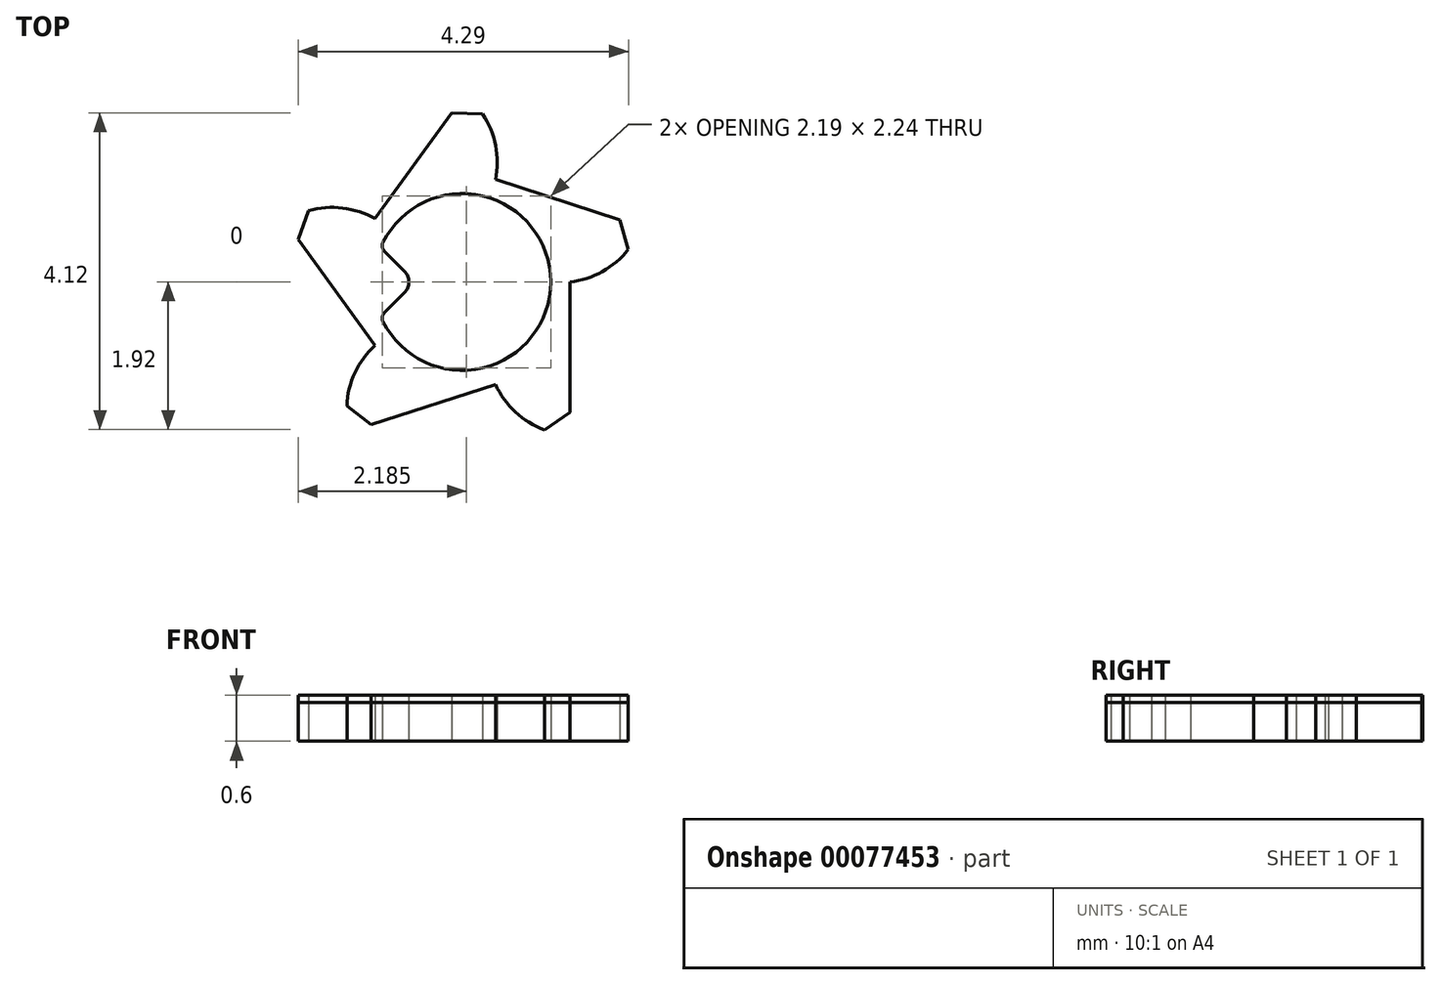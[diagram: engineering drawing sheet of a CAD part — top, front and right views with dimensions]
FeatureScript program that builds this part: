
annotation { "Feature Type Name" : "Feature", "Feature Type Description" : "" }
export const myFeature = defineFeature(function(context is Context, id is Id, definition is map)
    precondition{}
    {
        {
            var Q0;
            Q0=qCreatedBy(makeId("Top.planeOp"),FACE);
            var sketch = newSketch(context, id + "F0", { "sketchPlane" : qUnion([Q0])});
            skCircle(sketch, "E0", {"center": v(0, 0) * mm, "radius": 1.4 * mm, "construction": true});
            skCircle(sketch, "E1", {"center": v(0, 0) * mm, "radius": 1.65 * mm, "construction": true});
            skCircle(sketch, "E2", {"center": v(0, 0) * mm, "radius": 2.2 * mm, "construction": true});
            skArc(sketch, "E3", {"start": v(-1.03, -0.51) * mm, "mid": v(1.15, 0) * mm, "end": v(-1.03, 0.51) * mm});
            skLineSegment(sketch, "E4", {"start": v(0, 0) * mm, "end": v(1.4, 0) * mm, "construction": true});
            skLineSegment(sketch, "E5", {"start": v(0, 0) * mm, "end": v(0.43, -1.33) * mm, "construction": true});
            skLineSegment(sketch, "E6", {"start": v(0, 0) * mm, "end": v(-1.13, -0.82) * mm, "construction": true});
            skLineSegment(sketch, "E7", {"start": v(0, 0) * mm, "end": v(-1.13, 0.82) * mm, "construction": true});
            skLineSegment(sketch, "E8", {"start": v(0, 0) * mm, "end": v(0.43, 1.33) * mm, "construction": true});
            skLineSegment(sketch, "E9", {"start": v(1.4, 0) * mm, "end": v(1.4, -1.7) * mm});
            skLineSegment(sketch, "E10", {"start": v(1.4, -1.7) * mm, "end": v(1.07, -1.92) * mm});
            skLineSegment(sketch, "E11", {"start": v(0.43, -1.33) * mm, "end": v(-1.18, -1.86) * mm});
            skLineSegment(sketch, "E12", {"start": v(-1.18, -1.86) * mm, "end": v(-1.5, -1.61) * mm});
            skLineSegment(sketch, "E13", {"start": v(-1.13, -0.82) * mm, "end": v(-2.13, 0.55) * mm});
            skLineSegment(sketch, "E14", {"start": v(-2.13, 0.55) * mm, "end": v(-2, 0.93) * mm});
            skLineSegment(sketch, "E15", {"start": v(-1.13, 0.82) * mm, "end": v(-0.14, 2.2) * mm});
            skLineSegment(sketch, "E16", {"start": v(-0.14, 2.2) * mm, "end": v(0.26, 2.18) * mm});
            skLineSegment(sketch, "E17", {"start": v(0.43, 1.33) * mm, "end": v(2.05, 0.8) * mm});
            skLineSegment(sketch, "E18", {"start": v(2.05, 0.8) * mm, "end": v(2.16, 0.42) * mm});
            skArc(sketch, "E19", {"start": v(0.43, -1.33) * mm, "mid": v(0.7, -1.7) * mm, "end": v(1.07, -1.92) * mm});
            skPoint(sketch, "E19.third.point", {"position": v(0.36, -1.1) * mm});
            skArc(sketch, "E20", {"start": v(-1.13, -0.82) * mm, "mid": v(-1.4, -1.18) * mm, "end": v(-1.5, -1.61) * mm});
            skPoint(sketch, "E20.third.point", {"position": v(-0.93, -0.68) * mm});
            skPoint(sketch, "E21.third.point", {"position": v(-0.93, 0.68) * mm});
            skPoint(sketch, "E22.third.point", {"position": v(0.36, 1.1) * mm});
            skArc(sketch, "E23", {"start": v(1.4, 0) * mm, "mid": v(1.82, 0.14) * mm, "end": v(2.16, 0.42) * mm});
            skPoint(sketch, "E23.third.point", {"position": v(1.15, 0) * mm});
            skArc(sketch, "E24.trimOffspring", {"start": v(0.43, 1.33) * mm, "mid": v(0.43, 1.77) * mm, "end": v(0.26, 2.18) * mm});
            skLineSegment(sketch, "E25", {"start": v(0, 0) * mm, "end": v(-0.61, 0) * mm, "construction": true});
            skLineSegment(sketch, "E26", {"start": v(-0.75, 0.14) * mm, "end": v(-1, 0.4) * mm});
            skLineSegment(sketch, "E27", {"start": v(-0.75, -0.14) * mm, "end": v(-1, -0.4) * mm});
            skPoint(sketch, "E28.visualSharp", {"position": v(-0.61, 0) * mm});
            skArc(sketch, "E28.filletArc", {"start": v(-0.75, -0.14) * mm, "mid": v(-0.7, 0) * mm, "end": v(-0.75, 0.14) * mm});
            skPoint(sketch, "E29.visualSharp", {"position": v(-1.06, 0.45) * mm});
            skArc(sketch, "E29.filletArc", {"start": v(-1.03, 0.51) * mm, "mid": v(-1.04, 0.45) * mm, "end": v(-1, 0.4) * mm});
            skPoint(sketch, "E30.visualSharp", {"position": v(-1.06, -0.45) * mm});
            skArc(sketch, "E30.filletArc", {"start": v(-1, -0.4) * mm, "mid": v(-1.04, -0.45) * mm, "end": v(-1.03, -0.51) * mm});
            skLineSegment(sketch, "E31", {"start": v(0, 0) * mm, "end": v(-2.17, 0.34) * mm, "construction": true});
            skArc(sketch, "E32", {"start": v(-1.13, 0.82) * mm, "mid": v(-1.55, 0.96) * mm, "end": v(-2, 0.93) * mm});
            skSolve(sketch);
        }
        {
            var Q0;
            Q0=makeQuery(id+"F0.imprint","IMPRINT",FACE,{"disambiguationData":[TD([[makeQuery(id+"F0.imprint","IMPRINT",EDGE,{"derivedFrom":sQuery(id+"F0.wireOp",EDGE,"E3")}),-1.0]])]});
            extrude(context, id + "F1", {"entities" : qUnion([Q0]), "depth" : 0.5 * mm});
        }
        {
            var Q0;
            Q0=makeQuery(id+"F0.imprint","IMPRINT",FACE,{"disambiguationData":[TD([[makeQuery(id+"F0.imprint","IMPRINT",EDGE,{"derivedFrom":sQuery(id+"F0.wireOp",EDGE,"E3")}),-1.0]])]});
            extrude(context, id + "F2", {"entities" : qUnion([Q0]), "depth" : 0.6 * mm});
        }
    });
